# Revit family: Shower-Handshower-KOHLER-Purist-K-973
name_source: partatom
category: Plumbing Fixtures
revit_build: Autodesk Revit 2015 (Build: 20140606_1530(x64)
units: mm (PartAtom-declared; Revit-internal decimal feet)

## types (4) — shared parameters
ADA Compliant = Yes
Assembly Code = C1030200
Cold Water Diameter = 1/2"
Date Modified = 09/18/2017
Default Elevation = 42"
Description = Purist®Multi-function Handshower K-973
Flow Rate = 3 GPM
HW Connection = No
Height = 11 7/16"
Inlet Connection = Inlet Connection
Length = 4 9/16"
Manufacturer = Kohler
MasterFormat 1995 = 15410
MasterFormat 2004 = 22.41.39
Material = KOHLER finishes resist corrosion and tarnish
Outlet Connection = Outlet Connection
Pressure = 0.00 psi
Product Documentation Link = http://www.us.kohler.com
Product Name = Purist
Product Page URL = http://www.us.kohler.com
URL = http://www.us.kohler.com
Waste Connection Diameter = 0"
Width = 3 5/8"

## per-type parameters (varying)
| type | CW Connection | Finish | Model | Type |
| CP-Polished Chrome | No | Metal-Kohler-CP-Polished Chrome | K-973-CP-Polished Chrome | 1 |
| SN-Vibrant Polished Nickel | Yes | Metal-Kohler-SN-Vibrant Polished Nickel | K-973-SN-Vibrant Polished Nickel | 2 |
| BN-Vibrant Brushed Nickel | Yes | Metal-Kohler-BN-Vibrant Brushed Nickel | K-973-BN_Vibrant Brushed Nickel | 3 |
| BV-Vibrant Brushed Bronze | Yes | Metal-Kohler-BV-Vibrant Brushed Bronze | K-973-BV-Vibrant Brushed Bronze | 4 |

## geometry (parser evidence)
native form markers: Sweep x5
no freeform markers — native parametric forms only
